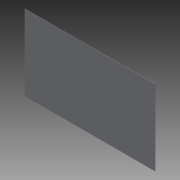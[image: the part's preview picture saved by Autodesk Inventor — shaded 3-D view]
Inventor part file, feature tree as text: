
AUTODESK INVENTOR PART (.ipt)
format: ipt  version: 2013 (Build 170138000, 138)  size: 69,632 bytes
history: native  units: in
note: dims shown in document units (in); Inventor stores cm internally (conversion verified against a paired STEP export)
features: extrude x1, sketch x1
ambient origin geometry x8: Origin, YZ Plane, XZ Plane, XY Plane, X Axis, Y Axis, Z Axis, Center Point
bodies: Solid1 (feature_tree)
feature tree (2):
  extrude  "Extrusion1"  Depth=42.0in
  sketch  "Sketch1"  dims[d0=72.5in d1=42.0in d2=0.125in d3=0.0in]
